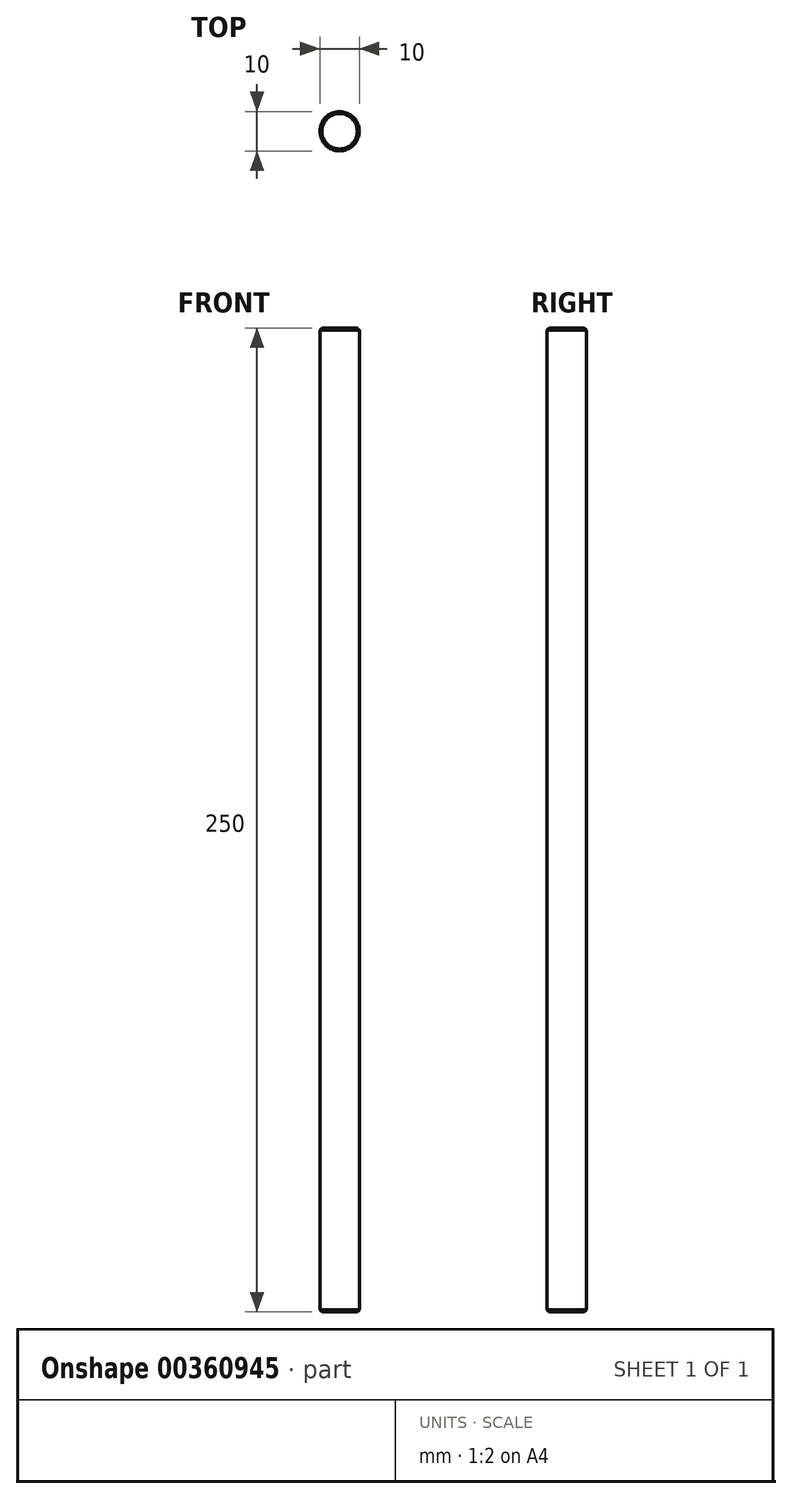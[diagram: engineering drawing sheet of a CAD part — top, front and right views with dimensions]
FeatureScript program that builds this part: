
annotation { "Feature Type Name" : "Feature", "Feature Type Description" : "" }
export const myFeature = defineFeature(function(context is Context, id is Id, definition is map)
    precondition{}
    {
        {
            var Q0;
            Q0=qCreatedBy(makeId("Top.planeOp"),FACE);
            var sketch = newSketch(context, id + "F0", { "sketchPlane" : qUnion([Q0])});
            skCircle(sketch, "E0", {"center": v(0, 0) * mm, "radius": 5 * mm});
            skSolve(sketch);
        }
        {
            var Q0;
            Q0=qSketchRegion(id+"F0",true);
            extrude(context, id + "F1", {"entities" : qUnion([Q0]), "depth" : 250 * mm});
        }
        {
            var Q0;
            Q0=makeQuery(id+"F1.opExtrude","CAP_FACE",FACE,{"disambiguationData":[OSD([sQuery(id+"F0.wireOp",EDGE,"E0")])],"isStart":false});
            var Q1;
            Q1=makeQuery(id+"F1.opExtrude","CAP_FACE",FACE,{"disambiguationData":[OSD([sQuery(id+"F0.wireOp",EDGE,"E0")])],"isStart":true});
            chamfer(context, id + "F2", {"entities" : qUnion([Q0, Q1]), "width" : 0.5 * mm, "tangentPropagation" : true});
        }
    });
